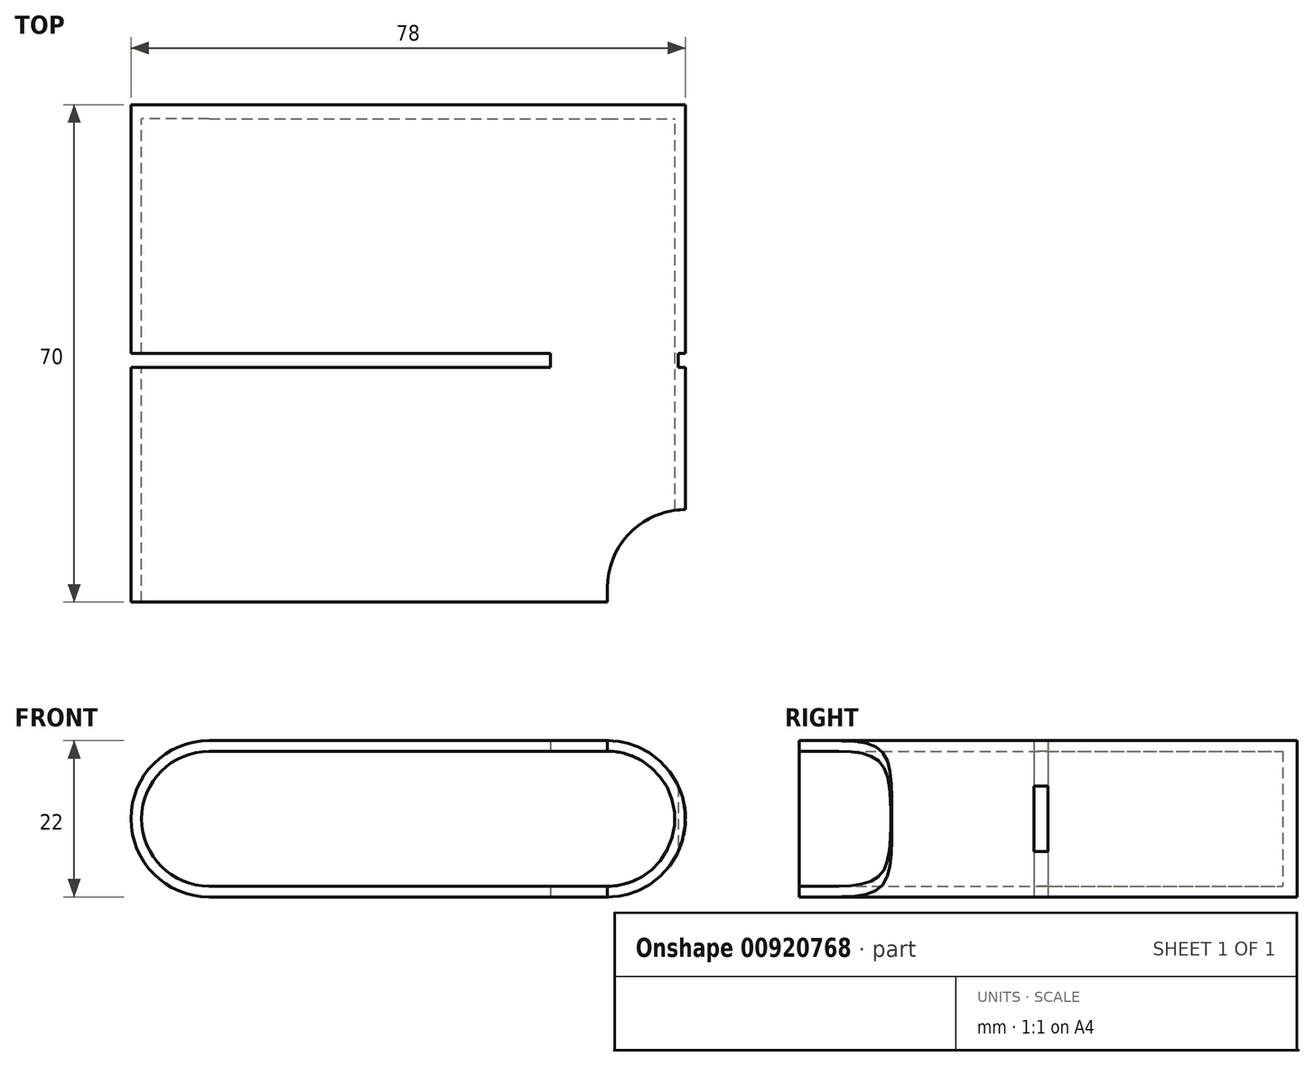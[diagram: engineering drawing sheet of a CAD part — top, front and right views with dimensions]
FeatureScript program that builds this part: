
annotation { "Feature Type Name" : "Feature", "Feature Type Description" : "" }
export const myFeature = defineFeature(function(context is Context, id is Id, definition is map)
    precondition{}
    {
        {
            var Q0;
            Q0=qCreatedBy(makeId("Front.planeOp"),FACE);
            var sketch = newSketch(context, id + "F0", { "sketchPlane" : qUnion([Q0])});
            skArc(sketch, "E0", {"start": v(0, 11) * mm, "mid": v(-11, 0) * mm, "end": v(0, -11) * mm});
            skArc(sketch, "E1", {"start": v(56, -11) * mm, "mid": v(67, 0) * mm, "end": v(56, 11) * mm});
            skLineSegment(sketch, "E2", {"start": v(0, 11) * mm, "end": v(56, 11) * mm});
            skLineSegment(sketch, "E3", {"start": v(0, -11) * mm, "end": v(56, -11) * mm});
            skLineSegment(sketch, "E4.0", {"start": v(0, 9.5) * mm, "end": v(56, 9.5) * mm});
            skArc(sketch, "E4.1", {"start": v(0, 9.5) * mm, "mid": v(-9.5, 0) * mm, "end": v(0, -9.5) * mm});
            skLineSegment(sketch, "E4.2", {"start": v(0, -9.5) * mm, "end": v(56, -9.5) * mm});
            skArc(sketch, "E4.3", {"start": v(56, -9.5) * mm, "mid": v(65.5, 0) * mm, "end": v(56, 9.5) * mm});
            skSolve(sketch);
        }
        {
            var Q0;
            Q0 = qSketchRegion(id + "F0", true);
            extrude(context, id + "F1", {"entities" : qUnion([Q0]), "depth" : 70 * mm, "offsetDistance" : 25 * mm});
        }
        {
            var Q0;
            Q0=makeQuery(id+"F0.imprint","IMPRINT",FACE,{"disambiguationData":[TD([[makeQuery(id+"F0.imprint","IMPRINT",EDGE,{"derivedFrom":sQuery(id+"F0.wireOp",EDGE,"E4.0")}),-1.0]])]});
            extrude(context, id + "F2", {"entities" : qUnion([Q0]), "operationType" : NewBodyOperationType.ADD, "depth" : 2 * mm, "offsetDistance" : 25 * mm});
        }
        {
            var Q0;
            Q0=makeQuery(id+"F1.opExtrude","SWEPT_FACE",FACE,{"disambiguationData":[OSD([sQuery(id+"F0.wireOp",EDGE,"E3")])]});
            var sketch = newSketch(context, id + "F3", { "sketchPlane" : qUnion([Q0])});
            skLineSegment(sketch, "E5", {"start": v(56, 70) * mm, "end": v(56, 68) * mm});
            skLineSegment(sketch, "E6", {"start": v(67, 57) * mm, "end": v(67, 57) * mm});
            skPoint(sketch, "E7.visualSharp", {"position": v(56, 57) * mm});
            skArc(sketch, "E7.filletArc", {"start": v(56, 68) * mm, "mid": v(59.22, 60.22) * mm, "end": v(67, 57) * mm});
            skLineSegment(sketch, "E8", {"start": v(56, 70) * mm, "end": v(67, 70) * mm});
            skLineSegment(sketch, "E9", {"start": v(67, 70) * mm, "end": v(67, 57) * mm});
            skSolve(sketch);
        }
        {
            var Q0;
            Q0 = qSketchRegion(id + "F3", true);
            extrude(context, id + "F4", {"entities" : qUnion([Q0]), "operationType" : NewBodyOperationType.REMOVE, "oppositeDirection" : true, "depth" : 25 * mm, "offsetDistance" : 25 * mm});
        }
        {
            var Q0;
            Q0=makeQuery(id+"F1.opExtrude","SWEPT_FACE",FACE,{"disambiguationData":[OSD([sQuery(id+"F0.wireOp",EDGE,"E3")])]});
            var sketch = newSketch(context, id + "F5", { "sketchPlane" : qUnion([Q0])});
            skLineSegment(sketch, "E10.bottom", {"start": v(48, 37) * mm, "end": v(-13, 37) * mm});
            skLineSegment(sketch, "E10.top", {"start": v(48, 35) * mm, "end": v(-13, 35) * mm});
            skLineSegment(sketch, "E10.left", {"start": v(48, 37) * mm, "end": v(48, 35) * mm});
            skLineSegment(sketch, "E10.right", {"start": v(-13, 37) * mm, "end": v(-13, 35) * mm});
            skLineSegment(sketch, "E11.bottom", {"start": v(66, 37) * mm, "end": v(68, 37) * mm});
            skLineSegment(sketch, "E11.top", {"start": v(66, 35) * mm, "end": v(68, 35) * mm});
            skLineSegment(sketch, "E11.left", {"start": v(66, 37) * mm, "end": v(66, 35) * mm});
            skLineSegment(sketch, "E11.right", {"start": v(68, 37) * mm, "end": v(68, 35) * mm});
            skSolve(sketch);
        }
        {
            var Q0;
            Q0 = qSketchRegion(id + "F5", true);
            extrude(context, id + "F6", {"entities" : qUnion([Q0]), "operationType" : NewBodyOperationType.REMOVE, "oppositeDirection" : true, "depth" : 25 * mm, "offsetDistance" : 25 * mm});
        }
    });
